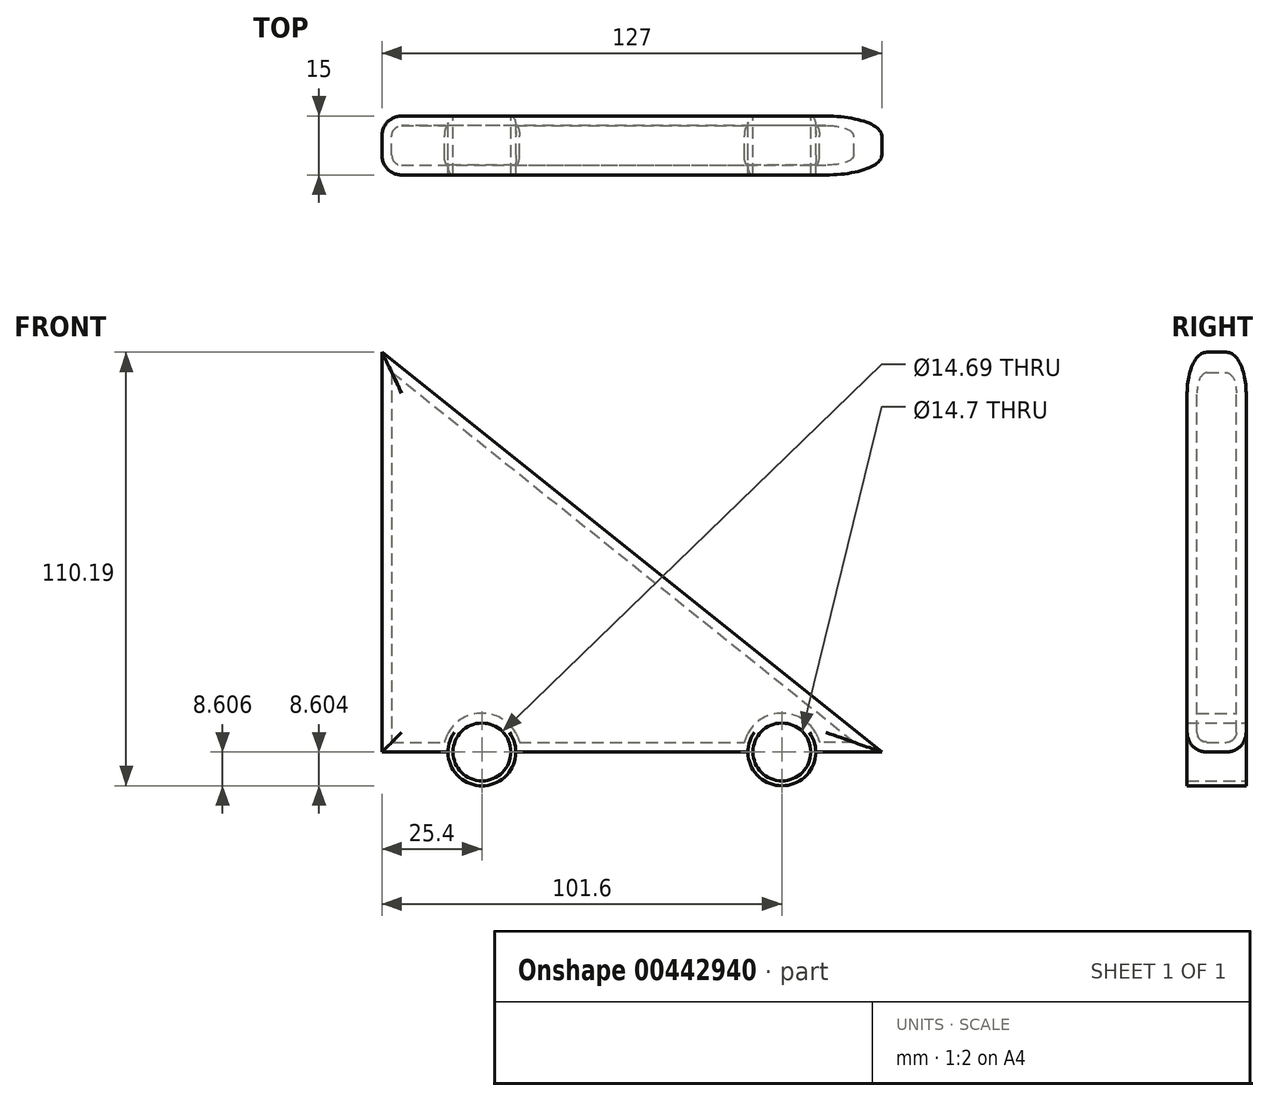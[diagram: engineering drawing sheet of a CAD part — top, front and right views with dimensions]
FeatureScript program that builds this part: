
annotation { "Feature Type Name" : "Feature", "Feature Type Description" : "" }
export const myFeature = defineFeature(function(context is Context, id is Id, definition is map)
    precondition{}
    {
        {
            var Q0;
            Q0=qCreatedBy(makeId("Front.planeOp"),FACE);
            var sketch = newSketch(context, id + "F0", { "sketchPlane" : qUnion([Q0])});
            skLineSegment(sketch, "E0", {"start": v(-70.3, 50.53) * mm, "end": v(-70.3, -51.07) * mm});
            skLineSegment(sketch, "E1", {"start": v(56.7, -51.07) * mm, "end": v(-70.3, 50.53) * mm});
            skLineSegment(sketch, "E2", {"start": v(-70.3, -51.07) * mm, "end": v(-44.9, -51.07) * mm});
            skLineSegment(sketch, "E3", {"start": v(56.7, -51.07) * mm, "end": v(31.3, -51.07) * mm});
            skArc(sketch, "E4", {"start": v(-53.5, -51.07) * mm, "mid": v(-44.9, -42.47) * mm, "end": v(-36.3, -51.07) * mm});
            skArc(sketch, "E5", {"start": v(39.9, -51.07) * mm, "mid": v(31.3, -42.47) * mm, "end": v(22.7, -51.07) * mm});
            skLineSegment(sketch, "E6", {"start": v(-36.3, -51.07) * mm, "end": v(22.7, -51.07) * mm});
            skArc(sketch, "E7", {"start": v(-53.5, -51.07) * mm, "mid": v(-44.9, -59.66) * mm, "end": v(-36.3, -51.07) * mm});
            skArc(sketch, "E8", {"start": v(22.7, -51.07) * mm, "mid": v(31.3, -59.65) * mm, "end": v(39.9, -51.07) * mm});
            skCircle(sketch, "E9", {"center": v(-44.9, -51.06) * mm, "radius": 7.35 * mm});
            skCircle(sketch, "E10", {"center": v(31.3, -51.05) * mm, "radius": 7.35 * mm});
            skSolve(sketch);
        }
        {
            var Q0;
            Q0 = qSketchRegion(id + "F0", true);
            extrude(context, id + "F1", {"entities" : qUnion([Q0]), "depth" : 15 * mm});
        }
        {
            var Q0;
            Q0=makeQuery(id+"F1.opExtrude","CAP_EDGE",EDGE,{"disambiguationData":[OSD([sQuery(id+"F0.wireOp",EDGE,"E0")])],"isStart":false});
            var Q1;
            Q1=makeQuery(id+"F1.opExtrude","CAP_EDGE",EDGE,{"disambiguationData":[OSD([sQuery(id+"F0.wireOp",EDGE,"E1")])],"isStart":false});
            var Q2;
            Q2=makeQuery(id+"F1.opExtrude","CAP_EDGE",EDGE,{"disambiguationData":[OSD([sQuery(id+"F0.wireOp",EDGE,"E6")])],"isStart":false});
            var Q3;
            Q3=makeQuery(id+"F1.opExtrude","CAP_EDGE",EDGE,{"disambiguationData":[OSD([sQuery(id+"F0.wireOp",EDGE,"E2")])],"isStart":false});
            var Q4;
            Q4=makeQuery(id+"F1.opExtrude","CAP_EDGE",EDGE,{"disambiguationData":[OSD([sQuery(id+"F0.wireOp",EDGE,"E3")])],"isStart":false});
            fillet(context, id + "F2", {"entities" : qUnion([Q0, Q1, Q2, Q3, Q4]), "radius" : 5 * mm, "tangentPropagation" : true, "allowEdgeOverflow" : false});
        }
        {
            var Q0;
            Q0=makeQuery(id+"F1.opExtrude","CAP_EDGE",EDGE,{"disambiguationData":[OSD([sQuery(id+"F0.wireOp",EDGE,"E1")])],"isStart":true});
            var Q1;
            Q1=makeQuery(id+"F1.opExtrude","CAP_EDGE",EDGE,{"disambiguationData":[OSD([sQuery(id+"F0.wireOp",EDGE,"E6")])],"isStart":true});
            var Q2;
            Q2=makeQuery(id+"F1.opExtrude","CAP_EDGE",EDGE,{"disambiguationData":[OSD([sQuery(id+"F0.wireOp",EDGE,"E3")])],"isStart":true});
            var Q3;
            Q3=makeQuery(id+"F1.opExtrude","CAP_EDGE",EDGE,{"disambiguationData":[OSD([sQuery(id+"F0.wireOp",EDGE,"E0")])],"isStart":true});
            var Q4;
            Q4=makeQuery(id+"F1.opExtrude","CAP_EDGE",EDGE,{"disambiguationData":[OSD([sQuery(id+"F0.wireOp",EDGE,"E2")])],"isStart":true});
            fillet(context, id + "F3", {"entities" : qUnion([Q0, Q1, Q2, Q3, Q4]), "radius" : 5 * mm, "tangentPropagation" : true, "allowEdgeOverflow" : false});
        }
        {
            var Q0;
            Q0=makeQuery(id+"F2.opFillet","BLEND_FACE",FACE,{"disambiguationData":[OSD([sQuery(id+"F0.wireOp",EDGE,"E1")])]});
            var Q1;
            Q1=makeQuery(id+"F2.opFillet","BLEND_FACE",FACE,{"disambiguationData":[OSD([sQuery(id+"F0.wireOp",EDGE,"E0")])]});
            var Q2;
            Q2=makeQuery(id+"F2.opFillet","BLEND_FACE",FACE,{"disambiguationData":[OSD([sQuery(id+"F0.wireOp",EDGE,"E6")])]});
            var Q3;
            Q3=makeQuery(id+"F1.opExtrude","SWEPT_FACE",FACE,{"disambiguationData":[OSD([sQuery(id+"F0.wireOp",EDGE,"E4")])]});
            var Q4;
            Q4=makeQuery(id+"F1.opExtrude","SWEPT_FACE",FACE,{"disambiguationData":[OSD([sQuery(id+"F0.wireOp",EDGE,"E5")])]});
            var Q5;
            Q5=makeQuery(id+"F2.opFillet","BLEND_FACE",FACE,{"disambiguationData":[OSD([sQuery(id+"F0.wireOp",EDGE,"E2")])]});
            var Q6;
            Q6=makeQuery(id+"F3.opFillet","BLEND_FACE",FACE,{"disambiguationData":[OSD([sQuery(id+"F0.wireOp",EDGE,"E0")])]});
            var Q7;
            Q7=makeQuery(id+"F3.opFillet","BLEND_FACE",FACE,{"disambiguationData":[OSD([sQuery(id+"F0.wireOp",EDGE,"E1")])]});
            var Q8;
            Q8=makeQuery(id+"F1.opExtrude","CAP_FACE",FACE,{"disambiguationData":[OSD([sQuery(id+"F0.wireOp",EDGE,"E0"),sQuery(id+"F0.wireOp",EDGE,"E1"),sQuery(id+"F0.wireOp",EDGE,"E2"),sQuery(id+"F0.wireOp",EDGE,"E3"),sQuery(id+"F0.wireOp",EDGE,"E4"),sQuery(id+"F0.wireOp",EDGE,"E5"),sQuery(id+"F0.wireOp",EDGE,"E6")])],"isStart":true});
            var Q9;
            Q9=makeQuery(id+"F3.opFillet","BLEND_FACE",FACE,{"disambiguationData":[OSD([sQuery(id+"F0.wireOp",EDGE,"E3")])]});
            var Q10;
            Q10=makeQuery(id+"F1.opExtrude","SWEPT_FACE",FACE,{"disambiguationData":[OSD([sQuery(id+"F0.wireOp",EDGE,"E1")])]});
            var Q11;
            Q11=makeQuery(id+"F1.opExtrude","SWEPT_BODY",BODY,{"disambiguationData":[OSD([sQuery(id+"F0.wireOp",EDGE,"E0"),sQuery(id+"F0.wireOp",EDGE,"E1"),sQuery(id+"F0.wireOp",EDGE,"E2"),sQuery(id+"F0.wireOp",EDGE,"E3"),sQuery(id+"F0.wireOp",EDGE,"E4"),sQuery(id+"F0.wireOp",EDGE,"E5"),sQuery(id+"F0.wireOp",EDGE,"E6")])]});
            shell(context, id + "F4", {"isHollow" : true, "entities" : qUnion([Q0, Q1, Q2, Q3, Q4, Q5, Q6, Q7, Q8, Q9, Q10]), "parts" : qUnion([Q11]), "thickness" : 2.5 * mm});
        }
    });
